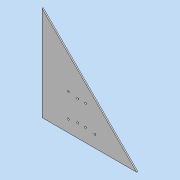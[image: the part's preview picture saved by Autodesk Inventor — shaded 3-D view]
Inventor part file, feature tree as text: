
AUTODESK INVENTOR PART (.ipt)
format: ipt  version: 2020 (Build 240168000, 168)  size: 100,352 bytes
history: native  units: mm
features: other x2, sketch x2, hole x1
ambient origin geometry x8: Origin, YZ Plane, XZ Plane, XY Plane, X Axis, Y Axis, Z Axis, Center Point
bodies: Body1 (feature_tree)
feature tree (5):
  other  "ソリッド1"
  hole  "穴1"  [1 undecoded]
  sketch  "スケッチ1"
  other  "プレート1"
  sketch  "スケッチ2"
note: 1 required parameter value undecoded (feature->parameter linkage not recoverable at this tier; creation-order binding heuristic only, values carry confidence <= 0.55)
